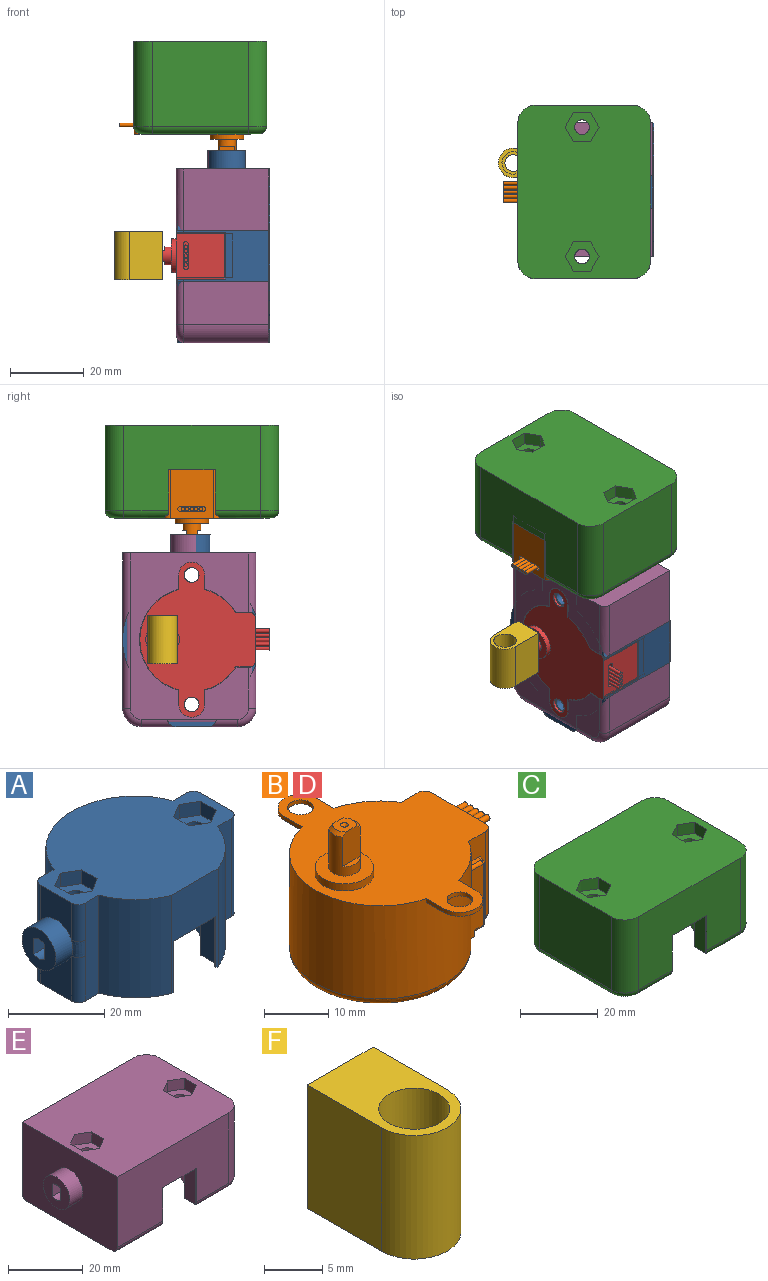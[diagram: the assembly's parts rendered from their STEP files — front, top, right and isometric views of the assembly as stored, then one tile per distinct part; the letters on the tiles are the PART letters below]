
ASSEMBLY  parts=6 mates=5
PART A: 70 faces, bbox 52x36x25 mm
  f0: plane 9.46x9.13mm, normal (-1,0,0), area 66.9mm2, adj f1,f59,f66,f69
  f1: plane 47x35.99mm, normal (0,0,1), area 1107mm2, adj f0,f4,f5,f6,f7,f8,f9,f10
  f2: cylinder r=2mm len=20.7mm, axis (0,0,-1), area 260.1mm2, adj f32,f51
  f3: cylinder r=2mm len=20.7mm, axis (0,0,-1), area 260.1mm2, adj f31,f44
  f4: plane 25x13.75mm, normal (0,-1,0), area 180.1mm2, adj f1,f5,f15,f16,f52,f53,f54
  f5: cylinder r=18.67mm len=25mm, axis (0,0,-1), area 388.4mm2, adj f1,f4,f6,f16
  f6: plane 25x4.03mm, normal (0,-1,0), area 100.9mm2, adj f1,f5,f16,f62
  f7: plane 25x9.13mm, normal (1,0,0), area 228.2mm2, adj f1,f16,f62,f63
  f8: plane 25x4mm, normal (0,1,0), area 100mm2, adj f1,f9,f16,f63
  f9: cylinder r=18.67mm len=25mm, axis (0,0,-1), area 533.3mm2, adj f1,f8,f10,f16
  f10: plane 25x2.68mm, normal (0,1,0), area 67.1mm2, adj f1,f9,f11,f16
  f11: cylinder r=18.67mm len=25mm, axis (0,0,-1), area 533.3mm2, adj f1,f10,f12,f16
  f12: plane 25x4.05mm, normal (0,1,0), area 100.1mm2, adj f1,f11,f16,f64,f65,f66
  f13: plane 11.46x9.13mm, normal (-1,0,0), area 85.1mm2, adj f16,f59,f64,f67
  f14: plane 25x4.08mm, normal (0,-1,0), area 101mm2, adj f1,f15,f16,f67,f68,f69
  f15: cylinder r=18.67mm len=25mm, axis (0,0,-1), area 388.4mm2, adj f1,f4,f14,f16
  f16: plane 47x35.99mm, normal (0,0,-1), area 453.8mm2, adj f4,f5,f6,f7,f8,f9,f10,f11
  f17: sphere r=1mm, area 1.6mm2, adj f18,f22,f23
  f18: cylinder r=1mm len=13mm, axis (0,0,1), area 20.4mm2, adj f16,f17,f24,f53
  f19: sphere r=1mm, area 1.6mm2, adj f20,f21,f22
  f20: cylinder r=1mm len=13mm, axis (0,0,1), area 20.4mm2, adj f16,f19,f28,f52
  f21: cylinder r=1mm len=4.05mm, axis (0,-1,0), area 5.9mm2, adj f19,f26,f28,f29
  f22: cylinder r=1mm len=12.6mm, axis (-1,0,0), area 19.8mm2, adj f17,f19,f29,f54
  f23: cylinder r=1mm len=4.05mm, axis (0,1,0), area 5.9mm2, adj f17,f24,f26,f29
  f24: plane 13x4.05mm, normal (1,0,0), area 52.7mm2, adj f16,f18,f23,f26
  f25: torus R=13mm, axis (0,0,-1), area 134.6mm2, adj f26,f27
  f26: cylinder r=14mm len=28mm, axis (0,0,1), area 1358.2mm2, adj f16,f21,f23,f24,f25,f28,f29,f30
  f27: plane 26x26mm, normal (0,0,-1), area 530.9mm2, adj f25
  f28: plane 13x4.05mm, normal (-1,0,0), area 52.7mm2, adj f16,f20,f21,f26
  f29: plane 12.6x3.5mm, normal (0,0,-1), area 31.3mm2, adj f21,f22,f23,f26
  f30: plane 3.94x0.8mm, normal (0,1,0), area 3.2mm2, adj f16,f26,f31,f35
  f31: plane 7.44x7mm, normal (0,0,-1), area 32.2mm2, adj f3,f26,f30,f33,f35
  f32: plane 7.44x7mm, normal (0,0,-1), area 32.2mm2, adj f2,f26,f34,f36,f37
  f33: plane 3.94x0.8mm, normal (0,-1,0), area 3.2mm2, adj f16,f26,f31,f35
  f34: plane 3.94x0.8mm, normal (0,-1,0), area 3.2mm2, adj f16,f26,f32,f37
  f35: cylinder r=3.5mm len=7mm, axis (0,0,1), area 8.8mm2, adj f16,f30,f31,f33
  f36: plane 3.94x0.8mm, normal (0,1,0), area 3.2mm2, adj f16,f26,f32,f37
  f37: cylinder r=3.5mm len=7mm, axis (0,0,1), area 8.8mm2, adj f16,f32,f34,f36
  f38: plane 3.98x3.5mm, normal (-0.5,-0.87,0), area 16.1mm2, adj f1,f39,f43,f44
  f39: plane 3.98x3.5mm, normal (0.5,-0.87,0), area 16.1mm2, adj f1,f38,f40,f44
  f40: plane 4.6x3.5mm, normal (1,0,0), area 16.1mm2, adj f1,f39,f41,f44
  f41: plane 3.98x3.5mm, normal (0.5,0.87,0), area 16.1mm2, adj f1,f40,f42,f44
  f42: plane 3.98x3.5mm, normal (-0.5,0.87,0), area 16.1mm2, adj f1,f41,f43,f44
  f43: plane 4.6x3.5mm, normal (-1,0,0), area 16.1mm2, adj f1,f38,f42,f44
  f44: plane 9.2x7.97mm, normal (0,0,1), area 42.4mm2, adj f3,f38,f39,f40,f41,f42,f43
  f45: plane 3.98x3.5mm, normal (-0.5,-0.87,0), area 16.1mm2, adj f1,f46,f50,f51
  f46: plane 3.98x3.5mm, normal (0.5,-0.87,0), area 16.1mm2, adj f1,f45,f47,f51
  f47: plane 4.6x3.5mm, normal (1,0,0), area 16.1mm2, adj f1,f46,f48,f51
  f48: plane 3.98x3.5mm, normal (0.5,0.87,0), area 16.1mm2, adj f1,f47,f49,f51
  f49: plane 3.98x3.5mm, normal (-0.5,0.87,0), area 16.1mm2, adj f1,f48,f50,f51
  f50: plane 4.6x3.5mm, normal (-1,0,0), area 16.1mm2, adj f1,f45,f49,f51
  f51: plane 9.2x7.97mm, normal (0,0,1), area 42.4mm2, adj f2,f45,f46,f47,f48,f49,f50
  f52: plane 13x0.38mm, normal (-1,0,0), area 4.9mm2, adj f4,f16,f20,f54
  f53: plane 13x0.38mm, normal (1,0,0), area 4.9mm2, adj f4,f16,f18,f54
  f54: plane 12.6x0.38mm, normal (0,0,-1), area 4.8mm2, adj f4,f22,f52,f53
  f55: plane 5x4mm, normal (0,1,0), area 20mm2, adj f56,f58,f60,f61
  f56: cylinder r=2.5mm len=5mm, axis (1,0,0), area 16.1mm2, adj f55,f57,f60,f61
  f57: plane 5x4mm, normal (0,-1,0), area 20mm2, adj f56,f58,f60,f61
  f58: cylinder r=2.5mm len=5mm, axis (1,0,0), area 16.1mm2, adj f55,f57,f60,f61
  f59: cylinder r=5mm len=10mm, axis (1,0,0), area 157.1mm2, adj f0,f13,f60,f65,f68
  f60: plane 10x10mm, normal (-1,0,0), area 64.5mm2, adj f55,f56,f57,f58,f59
  f61: plane 5x3mm, normal (-1,0,0), area 14mm2, adj f55,f56,f57,f58
  f62: cylinder r=2mm len=25mm, axis (0,0,1), area 78.5mm2, adj f1,f6,f7,f16
  f63: cylinder r=2mm len=25mm, axis (0,0,-1), area 78.5mm2, adj f1,f7,f8,f16
  f64: cylinder r=2mm len=11.46mm, axis (0,0,-1), area 36mm2, adj f12,f13,f16,f65
  f65: bspline ~5.76x2.6mm, area 11.6mm2, adj f12,f59,f64,f66
  f66: cylinder r=2mm len=9.46mm, axis (0,0,-1), area 29.7mm2, adj f0,f1,f12,f65
  f67: cylinder r=2mm len=11.46mm, axis (0,0,1), area 36mm2, adj f13,f14,f16,f68
  f68: bspline ~5.08x2.24mm, area 11.6mm2, adj f14,f59,f67,f69
  f69: cylinder r=2mm len=9.46mm, axis (0,0,1), area 29.7mm2, adj f0,f1,f14,f68
PART B: 77 faces, bbox 36.6x42.1x28.7 mm
  f0: cylinder r=0.5mm len=5mm, axis (-1,0,0), area 15.7mm2, adj f1,f70
  f1: plane 1x1mm, normal (1,0,0), area 0.8mm2, adj f0
  f2: cylinder r=0.5mm len=5mm, axis (-1,0,0), area 15.7mm2, adj f3,f70
  f3: plane 1x1mm, normal (1,0,0), area 0.8mm2, adj f2
  f4: cylinder r=2.45mm len=7.4mm, axis (0,0,-1), area 63.9mm2, adj f5,f6,f8,f11,f12,f13,f14
  f5: cone r=1.85mm half-angle=45deg, axis (0,0,-1), area 2.9mm2, adj f4,f7,f12,f14
  f6: cone r=1.85mm half-angle=45deg, axis (0,0,-1), area 2.9mm2, adj f4,f7,f12,f14
  f7: plane 3.7x3mm, normal (0,0,1), area 8.6mm2, adj f5,f6,f9,f12,f14
  f8: plane 9.1x9.1mm, normal (0,0,1), area 46.2mm2, adj f4,f10
  f9: cone r=0.6mm half-angle=45deg, axis (0,0,1), area 1.6mm2, adj f7
  f10: cylinder r=4.55mm len=9.1mm, axis (0,0,-1), area 38.6mm2, adj f8,f29
  f11: plane 3.87x0.95mm, normal (0,0,1), area 2.6mm2, adj f4,f12
  f12: plane 6.31x3.98mm, normal (0,-1,0), area 23.5mm2, adj f4,f5,f6,f7,f11
  f13: plane 3.87x0.95mm, normal (0,0,1), area 2.6mm2, adj f4,f14
  f14: plane 6.31x3.98mm, normal (0,1,0), area 23.5mm2, adj f4,f5,f6,f7,f13
  f15: plane 15.2x11.8mm, normal (1,0,0), area 169.8mm2, adj f29,f44,f45,f46,f66,f67,f68,f69
  f16: cylinder r=14.1mm len=28.2mm, axis (0,0,1), area 1244mm2, adj f17,f18,f19,f20,f21,f22,f23,f28
  f17: plane 16.5x3.36mm, normal (0,0,-1), area 25.3mm2, adj f16,f38,f39,f41,f42,f45,f52,f54
  f18: plane 16.28x3.78mm, normal (0,1,0), area 27.3mm2, adj f16,f29,f32,f33,f44,f48,f55
  f19: plane 3.84x0.75mm, normal (-1,0,0), area 2.9mm2, adj f16,f25,f28,f29
  f20: plane 3.84x0.75mm, normal (-1,0,0), area 2.9mm2, adj f16,f23,f24,f29
  f21: plane 3.84x0.75mm, normal (1,0,0), area 2.9mm2, adj f16,f25,f28,f29
  f22: plane 3.84x0.75mm, normal (1,0,0), area 2.9mm2, adj f16,f23,f24,f29
  f23: plane 7.34x7mm, normal (0,0,-1), area 31.5mm2, adj f16,f20,f22,f24,f27
  f24: cylinder r=3.5mm len=7mm, axis (0,0,1), area 8.2mm2, adj f20,f22,f23,f29
  f25: cylinder r=3.5mm len=7mm, axis (0,0,1), area 8.2mm2, adj f19,f21,f28,f29
  f26: cylinder r=2mm len=4mm, axis (0,0,1), area 9.4mm2, adj f28,f29
  f27: cylinder r=2mm len=4mm, axis (0,0,1), area 9.4mm2, adj f23,f29
  f28: plane 7.34x7mm, normal (0,0,-1), area 31.5mm2, adj f16,f19,f21,f25,f26
  f29: plane 42x31.3mm, normal (0,0,1), area 677.5mm2, adj f10,f15,f16,f18,f19,f20,f21,f22
  f30: plane 25.2x25.2mm, normal (0,0,-1), area 498.8mm2, adj f47
  f31: plane 16.28x3.78mm, normal (0,-1,0), area 27.3mm2, adj f16,f29,f35,f36,f46,f58,f64
  f32: plane 2.73x0.85mm, normal (0,0,1), area 1.9mm2, adj f16,f18,f48,f49
  f33: plane 11.6x1.02mm, normal (0.94,0.35,0), area 12.7mm2, adj f18,f48,f51,f54
  f34: plane 12.85x2.8mm, normal (0,1,0), area 33.6mm2, adj f16,f39,f40,f49,f51,f52
  f35: plane 2.73x0.85mm, normal (0,0,1), area 1.9mm2, adj f16,f31,f57,f58
  f36: plane 11.6x1.02mm, normal (0.94,-0.35,0), area 12.7mm2, adj f31,f58,f61,f63
  f37: plane 12.85x2.8mm, normal (0,-1,0), area 33.6mm2, adj f16,f41,f43,f57,f60,f61
  f38: plane 0.75x0.75mm, normal (0,-1,0), area 0.6mm2, adj f16,f17,f39,f40
  f39: cylinder r=14.85mm len=7.25mm, axis (0,0,1), area 6mm2, adj f17,f34,f38,f40,f52
  f40: plane 7.25x3.71mm, normal (0,0,-1), area 5.9mm2, adj f16,f34,f38,f39
  f41: cylinder r=14.85mm len=7.25mm, axis (0,0,1), area 6mm2, adj f17,f37,f42,f43,f60
  f42: plane 0.75x0.75mm, normal (0,1,0), area 0.6mm2, adj f16,f17,f41,f43
  f43: plane 7.25x3.71mm, normal (0,0,-1), area 5.9mm2, adj f16,f37,f41,f42
  f44: cylinder r=1.5mm len=16.2mm, axis (0,0,-1), area 37.3mm2, adj f15,f18,f29,f56
  f45: cylinder r=1.5mm len=13.8mm, axis (0,-1,0), area 30.8mm2, adj f15,f17,f56,f65
  f46: cylinder r=1.5mm len=16.2mm, axis (0,0,1), area 37.3mm2, adj f15,f29,f31,f65
  f47: torus R=12.6mm, axis (0,0,-1), area 200.7mm2, adj f16,f30
  f48: cylinder r=0.5mm len=1.2mm, axis (-0.35,0.94,0), area 0.8mm2, adj f18,f32,f33,f50
  f49: cylinder r=0.5mm len=2.8mm, axis (-1,0,0), area 2mm2, adj f16,f32,f34,f50
  f50: sphere r=0.5mm, area 0.3mm2, adj f48,f49,f51
  f51: cylinder r=0.5mm len=11.6mm, axis (0,0,-1), area 7.1mm2, adj f33,f34,f50,f53
  f52: cylinder r=0.5mm len=1.86mm, axis (-1,0,0), area 1.3mm2, adj f17,f34,f39,f53
  f53: sphere r=0.5mm, area 0.3mm2, adj f51,f52,f54
  f54: cylinder r=0.5mm len=1.52mm, axis (-0.35,0.94,0), area 1mm2, adj f17,f33,f53,f55
  f55: cylinder r=0.5mm len=1.35mm, axis (1,0,0), area 0.9mm2, adj f17,f18,f54,f56
  f56: bspline ~1.76x1.5mm, area 1.3mm2, adj f44,f45,f55
  f57: cylinder r=0.5mm len=2.8mm, axis (1,0,0), area 2mm2, adj f16,f35,f37,f59
  f58: cylinder r=0.5mm len=1.2mm, axis (0.35,0.94,0), area 0.8mm2, adj f31,f35,f36,f59
  f59: sphere r=0.5mm, area 0.3mm2, adj f57,f58,f61
  f60: cylinder r=0.5mm len=1.86mm, axis (1,0,0), area 1.3mm2, adj f17,f37,f41,f62
  f61: cylinder r=0.5mm len=11.6mm, axis (0,0,-1), area 7.1mm2, adj f36,f37,f59,f62
  f62: sphere r=0.5mm, area 0.3mm2, adj f60,f61,f63
  f63: cylinder r=0.5mm len=1.52mm, axis (0.35,0.94,0), area 1mm2, adj f17,f36,f62,f64
  f64: cylinder r=0.5mm len=1.35mm, axis (-1,0,0), area 0.9mm2, adj f17,f31,f63,f65
  f65: bspline ~1.76x1.5mm, area 1.3mm2, adj f45,f46,f64
  f66: plane 6.3x1mm, normal (0,0,1), area 6.3mm2, adj f15,f67,f69,f70
  f67: cylinder r=0.65mm len=1.3mm, axis (1,0,0), area 2mm2, adj f15,f66,f68,f70
  f68: plane 6.3x1mm, normal (0,0,-1), area 6.3mm2, adj f15,f67,f69,f70
  f69: cylinder r=0.65mm len=1.3mm, axis (1,0,0), area 2mm2, adj f15,f66,f68,f70
  f70: plane 7.6x1.3mm, normal (1,0,0), area 5.6mm2, adj f0,f2,f66,f67,f68,f69,f71,f73
  f71: cylinder r=0.5mm len=5mm, axis (-1,0,0), area 15.7mm2, adj f70,f72
  f72: plane 1x1mm, normal (1,0,0), area 0.8mm2, adj f71
  f73: cylinder r=0.5mm len=5mm, axis (-1,0,0), area 15.7mm2, adj f70,f74
  f74: plane 1x1mm, normal (1,0,0), area 0.8mm2, adj f73
  f75: cylinder r=0.5mm len=5mm, axis (-1,0,0), area 15.7mm2, adj f70,f76
  f76: plane 1x1mm, normal (1,0,0), area 0.8mm2, adj f75
PART C: 59 faces, bbox 47.8x36.8x25 mm
  f0: cylinder r=2mm len=12.24mm, axis (1,0,0), area 37.2mm2, adj f7,f8,f12,f20,f39,f56
  f1: plane 47x35.99mm, normal (0,0,1), area 1560mm2, adj f4,f5,f6,f7,f30,f31,f32,f33
  f2: cylinder r=2mm len=20.7mm, axis (0,0,-1), area 260.1mm2, adj f24,f55
  f3: cylinder r=2mm len=20.7mm, axis (0,0,-1), area 260.1mm2, adj f23,f48
  f4: plane 25.99x23mm, normal (1,0,0), area 597.7mm2, adj f1,f30,f33,f37
  f5: plane 37x23mm, normal (0,1,0), area 851mm2, adj f1,f30,f31,f34
  f6: plane 25.99x23mm, normal (-1,0,0), area 597.7mm2, adj f1,f31,f32,f38
  f7: plane 37x23mm, normal (0,-1,0), area 712.4mm2, adj f0,f1,f32,f33,f41,f56,f57,f58
  f8: plane 43x31.99mm, normal (0,0,-1), area 632.6mm2, adj f0,f16,f18,f20,f22,f25,f26,f27
  f9: sphere r=1mm, area 1.6mm2, adj f10,f14,f15
  f10: cylinder r=1mm len=12.9mm, axis (0,0,1), area 19.7mm2, adj f9,f16,f41,f57
  f11: sphere r=1mm, area 1.6mm2, adj f12,f13,f14
  f12: cylinder r=1mm len=12.9mm, axis (0,0,1), area 19.7mm2, adj f0,f11,f20,f56
  f13: cylinder r=1mm len=4.05mm, axis (0,-1,0), area 5.9mm2, adj f11,f18,f20,f21
  f14: cylinder r=1mm len=12.6mm, axis (-1,0,0), area 19.8mm2, adj f9,f11,f21,f58
  f15: cylinder r=1mm len=4.05mm, axis (0,1,0), area 5.9mm2, adj f9,f16,f18,f21
  f16: plane 13x4.05mm, normal (1,0,0), area 52.7mm2, adj f8,f10,f15,f18,f41
  f17: torus R=13mm, axis (0,0,-1), area 134.6mm2, adj f18,f19
  f18: cylinder r=14mm len=28mm, axis (0,0,1), area 1358.2mm2, adj f8,f13,f15,f16,f17,f20,f21,f22
  f19: plane 26x26mm, normal (0,0,-1), area 530.9mm2, adj f17
  f20: plane 13x4.05mm, normal (-1,0,0), area 52.7mm2, adj f0,f8,f12,f13,f18
  f21: plane 12.6x3.5mm, normal (0,0,-1), area 31.3mm2, adj f13,f14,f15,f18
  f22: plane 3.94x0.8mm, normal (0,1,0), area 3.2mm2, adj f8,f18,f23,f27
  f23: plane 7.44x7mm, normal (0,0,-1), area 32.2mm2, adj f3,f18,f22,f25,f27
  f24: plane 7.44x7mm, normal (0,0,-1), area 32.2mm2, adj f2,f18,f26,f28,f29
  f25: plane 3.94x0.8mm, normal (0,-1,0), area 3.2mm2, adj f8,f18,f23,f27
  f26: plane 3.94x0.8mm, normal (0,-1,0), area 3.2mm2, adj f8,f18,f24,f29
  f27: cylinder r=3.5mm len=7mm, axis (0,0,1), area 8.8mm2, adj f8,f22,f23,f25
  f28: plane 3.94x0.8mm, normal (0,1,0), area 3.2mm2, adj f8,f18,f24,f29
  f29: cylinder r=3.5mm len=7mm, axis (0,0,1), area 8.8mm2, adj f8,f24,f26,f28
  f30: cylinder r=5mm len=23mm, axis (0,0,1), area 180.6mm2, adj f1,f4,f5,f35
  f31: cylinder r=5mm len=23mm, axis (0,0,-1), area 180.6mm2, adj f1,f5,f6,f36
  f32: cylinder r=5mm len=23mm, axis (0,0,1), area 180.6mm2, adj f1,f6,f7,f40
  f33: cylinder r=5mm len=23mm, axis (0,0,-1), area 180.6mm2, adj f1,f4,f7,f39
  f34: cylinder r=2mm len=37mm, axis (-1,0,0), area 116.2mm2, adj f5,f8,f35,f36
  f35: torus R=3mm, axis (0,0,1), area 21.1mm2, adj f8,f30,f34,f37
  f36: torus R=3mm, axis (0,0,1), area 21.1mm2, adj f8,f31,f34,f38
  f37: cylinder r=2mm len=25.99mm, axis (0,1,0), area 81.6mm2, adj f4,f8,f35,f39
  f38: cylinder r=2mm len=25.99mm, axis (0,-1,0), area 81.6mm2, adj f6,f8,f36,f40
  f39: torus R=3mm, axis (0,0,1), area 21.1mm2, adj f0,f8,f33,f37
  f40: torus R=3mm, axis (0,0,1), area 21.1mm2, adj f8,f32,f38,f41
  f41: cylinder r=2mm len=12.16mm, axis (1,0,0), area 36.9mm2, adj f7,f8,f10,f16,f40,f57
  f42: plane 3.98x3.5mm, normal (-0.5,-0.87,0), area 16.1mm2, adj f1,f43,f47,f48
  f43: plane 3.98x3.5mm, normal (0.5,-0.87,0), area 16.1mm2, adj f1,f42,f44,f48
  f44: plane 4.6x3.5mm, normal (1,0,0), area 16.1mm2, adj f1,f43,f45,f48
  f45: plane 3.98x3.5mm, normal (0.5,0.87,0), area 16.1mm2, adj f1,f44,f46,f48
  f46: plane 3.98x3.5mm, normal (-0.5,0.87,0), area 16.1mm2, adj f1,f45,f47,f48
  f47: plane 4.6x3.5mm, normal (-1,0,0), area 16.1mm2, adj f1,f42,f46,f48
  f48: plane 9.2x7.97mm, normal (0,0,1), area 42.4mm2, adj f3,f42,f43,f44,f45,f46,f47
  f49: plane 3.98x3.5mm, normal (-0.5,-0.87,0), area 16.1mm2, adj f1,f50,f54,f55
  f50: plane 3.98x3.5mm, normal (0.5,-0.87,0), area 16.1mm2, adj f1,f49,f51,f55
  f51: plane 4.6x3.5mm, normal (1,0,0), area 16.1mm2, adj f1,f50,f52,f55
  f52: plane 3.98x3.5mm, normal (0.5,0.87,0), area 16.1mm2, adj f1,f51,f53,f55
  f53: plane 3.98x3.5mm, normal (-0.5,0.87,0), area 16.1mm2, adj f1,f52,f54,f55
  f54: plane 4.6x3.5mm, normal (-1,0,0), area 16.1mm2, adj f1,f49,f53,f55
  f55: plane 9.2x7.97mm, normal (0,0,1), area 42.4mm2, adj f2,f49,f50,f51,f52,f53,f54
  f56: plane 12.17x0.38mm, normal (-1,0,0), area 4.5mm2, adj f0,f7,f12,f58
  f57: plane 12.17x0.38mm, normal (1,0,0), area 4.5mm2, adj f7,f10,f41,f58
  f58: plane 12.6x0.38mm, normal (0,0,-1), area 4.8mm2, adj f7,f14,f56,f57
PART D: same geometry as B
PART E: 61 faces, bbox 52.4x36.8x25 mm
  f0: cylinder r=2mm len=12.24mm, axis (1,0,0), area 37.2mm2, adj f7,f8,f12,f20,f35,f51
  f1: plane 47x35.99mm, normal (0,0,1), area 1570.8mm2, adj f4,f5,f6,f7,f30,f31,f37,f38
  f2: cylinder r=2mm len=20.7mm, axis (0,0,-1), area 260.1mm2, adj f24,f50
  f3: cylinder r=2mm len=20.7mm, axis (0,0,-1), area 260.1mm2, adj f23,f43
  f4: plane 25.99x23mm, normal (1,0,0), area 597.7mm2, adj f1,f30,f31,f34
  f5: plane 42x23mm, normal (0,1,0), area 966mm2, adj f1,f6,f30,f32
  f6: plane 35.99x25mm, normal (-1,0,0), area 819.4mm2, adj f1,f5,f7,f8,f32,f36,f58
  f7: plane 42x23mm, normal (0,-1,0), area 827.4mm2, adj f0,f1,f6,f31,f36,f51,f52,f53
  f8: plane 45x31.99mm, normal (0,0,-1), area 700.5mm2, adj f0,f6,f16,f18,f20,f22,f25,f26
  f9: sphere r=1mm, area 1.6mm2, adj f10,f14,f15
  f10: cylinder r=1mm len=12.9mm, axis (0,0,1), area 19.7mm2, adj f9,f16,f36,f52
  f11: sphere r=1mm, area 1.6mm2, adj f12,f13,f14
  f12: cylinder r=1mm len=12.9mm, axis (0,0,1), area 19.7mm2, adj f0,f11,f20,f51
  f13: cylinder r=1mm len=4.05mm, axis (0,-1,0), area 5.9mm2, adj f11,f18,f20,f21
  f14: cylinder r=1mm len=12.6mm, axis (-1,0,0), area 19.8mm2, adj f9,f11,f21,f53
  f15: cylinder r=1mm len=4.05mm, axis (0,1,0), area 5.9mm2, adj f9,f16,f18,f21
  f16: plane 13x4.05mm, normal (1,0,0), area 52.7mm2, adj f8,f10,f15,f18,f36
  f17: torus R=13mm, axis (0,0,-1), area 134.6mm2, adj f18,f19
  f18: cylinder r=14mm len=28mm, axis (0,0,1), area 1358.2mm2, adj f8,f13,f15,f16,f17,f20,f21,f22
  f19: plane 26x26mm, normal (0,0,-1), area 530.9mm2, adj f17
  f20: plane 13x4.05mm, normal (-1,0,0), area 52.7mm2, adj f0,f8,f12,f13,f18
  f21: plane 12.6x3.5mm, normal (0,0,-1), area 31.3mm2, adj f13,f14,f15,f18
  f22: plane 3.94x0.8mm, normal (0,1,0), area 3.2mm2, adj f8,f18,f23,f27
  f23: plane 7.44x7mm, normal (0,0,-1), area 32.2mm2, adj f3,f18,f22,f25,f27
  f24: plane 7.44x7mm, normal (0,0,-1), area 32.2mm2, adj f2,f18,f26,f28,f29
  f25: plane 3.94x0.8mm, normal (0,-1,0), area 3.2mm2, adj f8,f18,f23,f27
  f26: plane 3.94x0.8mm, normal (0,-1,0), area 3.2mm2, adj f8,f18,f24,f29
  f27: cylinder r=3.5mm len=7mm, axis (0,0,1), area 8.8mm2, adj f8,f22,f23,f25
  f28: plane 3.94x0.8mm, normal (0,1,0), area 3.2mm2, adj f8,f18,f24,f29
  f29: cylinder r=3.5mm len=7mm, axis (0,0,1), area 8.8mm2, adj f8,f24,f26,f28
  f30: cylinder r=5mm len=23mm, axis (0,0,1), area 180.6mm2, adj f1,f4,f5,f33
  f31: cylinder r=5mm len=23mm, axis (0,0,-1), area 180.6mm2, adj f1,f4,f7,f35
  f32: cylinder r=2mm len=42mm, axis (-1,0,0), area 131.9mm2, adj f5,f6,f8,f33
  f33: torus R=3mm, axis (0,0,1), area 21.1mm2, adj f8,f30,f32,f34
  f34: cylinder r=2mm len=25.99mm, axis (0,1,0), area 81.6mm2, adj f4,f8,f33,f35
  f35: torus R=3mm, axis (0,0,1), area 21.1mm2, adj f0,f8,f31,f34
  f36: cylinder r=2mm len=17.16mm, axis (1,0,0), area 52.7mm2, adj f6,f7,f8,f10,f16,f52
  f37: plane 3.98x3.5mm, normal (-0.5,-0.87,0), area 16.1mm2, adj f1,f38,f42,f43
  f38: plane 3.98x3.5mm, normal (0.5,-0.87,0), area 16.1mm2, adj f1,f37,f39,f43
  f39: plane 4.6x3.5mm, normal (1,0,0), area 16.1mm2, adj f1,f38,f40,f43
  f40: plane 3.98x3.5mm, normal (0.5,0.87,0), area 16.1mm2, adj f1,f39,f41,f43
  f41: plane 3.98x3.5mm, normal (-0.5,0.87,0), area 16.1mm2, adj f1,f40,f42,f43
  f42: plane 4.6x3.5mm, normal (-1,0,0), area 16.1mm2, adj f1,f37,f41,f43
  f43: plane 9.2x7.97mm, normal (0,0,1), area 42.4mm2, adj f3,f37,f38,f39,f40,f41,f42
  f44: plane 3.98x3.5mm, normal (-0.5,-0.87,0), area 16.1mm2, adj f1,f45,f49,f50
  f45: plane 3.98x3.5mm, normal (0.5,-0.87,0), area 16.1mm2, adj f1,f44,f46,f50
  f46: plane 4.6x3.5mm, normal (1,0,0), area 16.1mm2, adj f1,f45,f47,f50
  f47: plane 3.98x3.5mm, normal (0.5,0.87,0), area 16.1mm2, adj f1,f46,f48,f50
  f48: plane 3.98x3.5mm, normal (-0.5,0.87,0), area 16.1mm2, adj f1,f47,f49,f50
  f49: plane 4.6x3.5mm, normal (-1,0,0), area 16.1mm2, adj f1,f44,f48,f50
  f50: plane 9.2x7.97mm, normal (0,0,1), area 42.4mm2, adj f2,f44,f45,f46,f47,f48,f49
  f51: plane 12.17x0.38mm, normal (-1,0,0), area 4.5mm2, adj f0,f7,f12,f53
  f52: plane 12.17x0.38mm, normal (1,0,0), area 4.5mm2, adj f7,f10,f36,f53
  f53: plane 12.6x0.38mm, normal (0,0,-1), area 4.8mm2, adj f7,f14,f51,f52
  f54: plane 5x4mm, normal (0,1,0), area 20mm2, adj f55,f57,f59,f60
  f55: cylinder r=2.5mm len=5mm, axis (1,0,0), area 16.1mm2, adj f54,f56,f59,f60
  f56: plane 5x4mm, normal (0,-1,0), area 20mm2, adj f55,f57,f59,f60
  f57: cylinder r=2.5mm len=5mm, axis (1,0,0), area 16.1mm2, adj f54,f56,f59,f60
  f58: cylinder r=5mm len=10mm, axis (1,0,0), area 157.1mm2, adj f6,f59
  f59: plane 10x10mm, normal (-1,0,0), area 64.5mm2, adj f54,f55,f56,f57,f58
  f60: plane 5x3mm, normal (-1,0,0), area 14mm2, adj f54,f55,f56,f57
PART F: 14 faces, bbox 8x13x13 mm
  f0: plane 13x8mm, normal (0,1,0), area 90mm2, adj f2,f3,f5,f6,f9,f10,f11,f12
  f1: cylinder r=4mm len=13mm, axis (0,0,-1), area 163.4mm2, adj f2,f3,f5,f6
  f2: plane 13x9mm, normal (1,0,0), area 117mm2, adj f0,f1,f5,f6
  f3: plane 13x9mm, normal (-1,0,0), area 117mm2, adj f0,f1,f5,f6
  f4: cylinder r=3.05mm len=12mm, axis (0,0,-1), area 230mm2, adj f5,f8
  f5: plane 13x8mm, normal (0,0,1), area 67.9mm2, adj f0,f1,f2,f3,f4
  f6: plane 13x8mm, normal (0,0,-1), area 81.2mm2, adj f0,f1,f2,f3,f7
  f7: cylinder r=2.25mm len=4.5mm, axis (0,0,-1), area 14.1mm2, adj f6,f8
  f8: plane 6.1x6.1mm, normal (0,0,1), area 13.3mm2, adj f4,f7
  f9: plane 5x4mm, normal (0,0,-1), area 20mm2, adj f0,f10,f12,f13
  f10: cylinder r=2.5mm len=5mm, axis (0,1,0), area 16.1mm2, adj f0,f9,f11,f13
  f11: plane 5x4mm, normal (0,0,1), area 20mm2, adj f0,f10,f12,f13
  f12: cylinder r=2.5mm len=5mm, axis (0,1,0), area 16.1mm2, adj f0,f9,f11,f13
  f13: plane 5x3mm, normal (0,1,0), area 14mm2, adj f9,f10,f11,f12
PLACE A rot(axis=(0,1,0),90deg) t=(-19.75,12.95,-43.89)mm
PLACE B rot(axis=(0,-1,0),180deg) t=(-6.25,12.89,-11.08)mm
PLACE C rot(axis=(0,0,-1),90deg) t=(-14.1,12.89,-10.88)mm
PLACE D rot(axis=(0.58,-0.58,-0.58),120deg) t=(-19.95,20.8,-43.89)mm
PLACE E rot(axis=(0,1,0),90deg) t=(-19.94,12.95,-43.89)mm
PLACE F rot(axis=(0,0,-1),90deg) t=(-32.7,20.8,-50.39)mm
MATE slider D.f16 <-> E.f17  axis (1,0,0) through (-0.75,12.95,-43.89)mm
MATE revolute A.f56 <-> B.f4  axis (0,0,1) through (-6.25,12.89,-20.43)mm
MATE fastened B.f16 <-> C.f17  axis (0,0,1) through (-14.1,12.89,8.12)mm
MATE fastened A.f25 <-> D.f16  axis (-1,0,0) through (-0.75,12.95,-43.89)mm
MATE revolute F.f12 <-> D.f4  axis (1,0,0) through (-28.7,20.8,-43.89)mm
